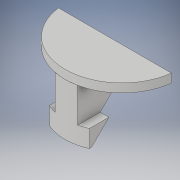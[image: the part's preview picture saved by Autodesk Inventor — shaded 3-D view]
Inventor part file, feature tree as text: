
AUTODESK INVENTOR PART (.ipt)
format: ipt  version: 2019 (Build 230136000, 136)  size: 138,752 bytes
history: native  units: mm
features: extrude x4, sketch x4, other x1, chamfer x1, mirror x1, projected_geometry x1
ambient origin geometry x8: Origin, YZ Plane, XZ Plane, XY Plane, X Axis, Y Axis, Z Axis, Center Point
bodies: Body1 (feature_tree)
feature tree (12):
  other  "Твердое тело1"
  extrude  "Выдавливание1"  Depth=4.6mm
  chamfer  "Фаска2"  Distance=5.0mm
  extrude  "Выдавливание3"  Depth=5.25mm
  mirror  "Зеркальное отражение1"
  extrude  "Выдавливание4"  Depth=5.0mm TaperAngle=45.0deg
  extrude  "Выдавливание5"  Depth=1.0mm
  sketch  "Эскиз1"
  sketch  "Эскиз3"
  sketch  "Эскиз4"
  projected_geometry  "Спроецированная петля1"
  sketch  "Эскиз5"
